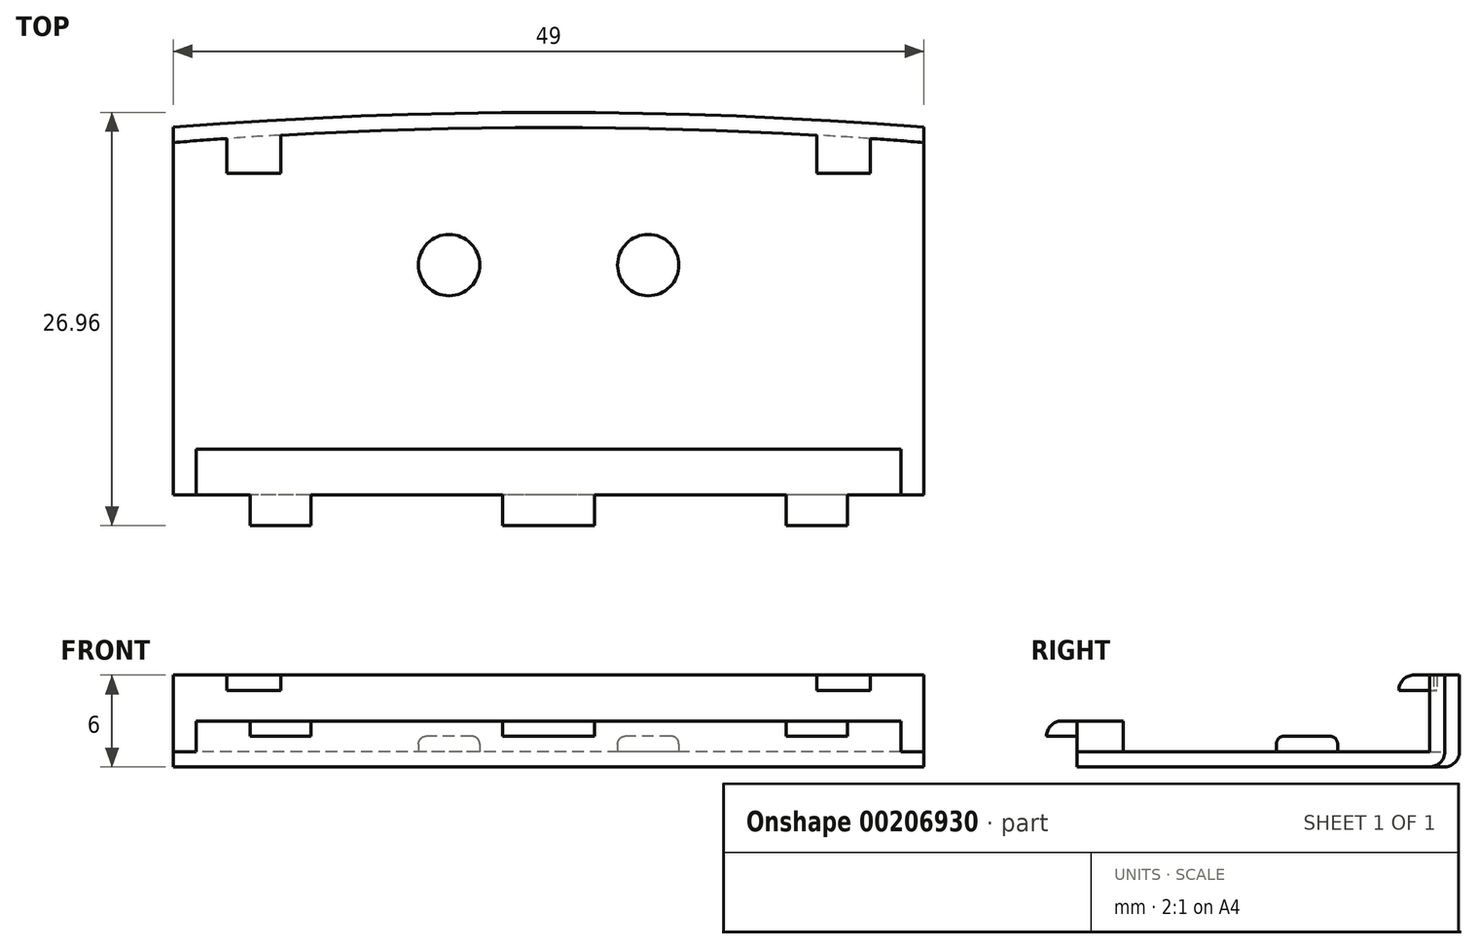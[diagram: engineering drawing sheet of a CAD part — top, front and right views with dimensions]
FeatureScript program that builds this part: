
annotation { "Feature Type Name" : "Feature", "Feature Type Description" : "" }
export const myFeature = defineFeature(function(context is Context, id is Id, definition is map)
    precondition{}
    {
        {
            var Q0;
            Q0=qCreatedBy(makeId("Top.planeOp"),FACE);
            var sketch = newSketch(context, id + "F0", { "sketchPlane" : qUnion([Q0])});
            skLineSegment(sketch, "E0.bottom", {"start": v(24.5, -12) * mm, "end": v(-24.5, -12) * mm});
            skLineSegment(sketch, "E0.left", {"start": v(24.5, -12) * mm, "end": v(24.5, 12) * mm});
            skLineSegment(sketch, "E0.right", {"start": v(-24.5, -12) * mm, "end": v(-24.5, 12) * mm});
            skPoint(sketch, "E0.middle", {"position": v(0, 0) * mm});
            skArc(sketch, "E1", {"start": v(24.5, 12) * mm, "mid": v(0, 12.96) * mm, "end": v(-24.5, 12) * mm});
            skArc(sketch, "E2", {"start": v(24.5, 11) * mm, "mid": v(0, 11.97) * mm, "end": v(-24.5, 11) * mm});
            skLineSegment(sketch, "E3.bottom", {"start": v(23, -9) * mm, "end": v(-23, -9) * mm});
            skLineSegment(sketch, "E3.left", {"start": v(23, -9) * mm, "end": v(23, -15) * mm});
            skLineSegment(sketch, "E3.right", {"start": v(-23, -9) * mm, "end": v(-23, -15) * mm});
            skPoint(sketch, "E3.middle", {"position": v(0, -12) * mm});
            skLineSegment(sketch, "E4.bottom", {"start": v(-16, -14) * mm, "end": v(-19.5, -14) * mm});
            skLineSegment(sketch, "E4.top", {"start": v(-16, -10) * mm, "end": v(-19.5, -10) * mm});
            skLineSegment(sketch, "E4.left", {"start": v(-16, -14) * mm, "end": v(-16, -10) * mm});
            skLineSegment(sketch, "E4.right", {"start": v(-19.5, -14) * mm, "end": v(-19.5, -10) * mm});
            skPoint(sketch, "E4.middle", {"position": v(-17.75, -12) * mm});
            skLineSegment(sketch, "E5.bottom", {"start": v(3, -14) * mm, "end": v(-3, -14) * mm});
            skLineSegment(sketch, "E5.top", {"start": v(3, -10) * mm, "end": v(-3, -10) * mm});
            skLineSegment(sketch, "E5.left", {"start": v(3, -14) * mm, "end": v(3, -10) * mm});
            skLineSegment(sketch, "E5.right", {"start": v(-3, -14) * mm, "end": v(-3, -10) * mm});
            skLineSegment(sketch, "E6.bottom", {"start": v(19.5, -14) * mm, "end": v(16, -14) * mm});
            skLineSegment(sketch, "E6.top", {"start": v(19.5, -10) * mm, "end": v(16, -10) * mm});
            skLineSegment(sketch, "E6.left", {"start": v(19.5, -14) * mm, "end": v(19.5, -10) * mm});
            skLineSegment(sketch, "E6.right", {"start": v(16, -14) * mm, "end": v(16, -10) * mm});
            skPoint(sketch, "E6.middle", {"position": v(17.75, -12) * mm});
            skCircle(sketch, "E7", {"center": v(-6.5, 3) * mm, "radius": 2 * mm});
            skCircle(sketch, "E8", {"center": v(6.5, 3) * mm, "radius": 2 * mm});
            skSolve(sketch);
        }
        {
            var Q0;
            {var subQ0=sQuery(id+"F0.wireOp",EDGE,"E1");Q0=makeQuery(id+"F0.imprint","IMPRINT",FACE,{"disambiguationData":[TD([[makeQuery(id+"F0.imprint","IMPRINT",EDGE,{"derivedFrom":subQ0}),1.0]])]});}
            var Q1;
            {var subQ3=sQuery(id+"F0.wireOp",EDGE,"E2");Q1=makeQuery(id+"F0.imprint","IMPRINT",FACE,{"disambiguationData":[TD([[makeQuery(id+"F0.imprint","IMPRINT",EDGE,{"derivedFrom":subQ3}),1.0]])]});}
            var Q2;
            {var subQ10=sQuery(id+"F0.wireOp",EDGE,"E3.bottom");Q2=makeQuery(id+"F0.imprint","IMPRINT",FACE,{"disambiguationData":[TD([[makeQuery(id+"F0.imprint","IMPRINT",EDGE,{"derivedFrom":subQ10}),1.0]])]});}
            var Q3;
            {var subQ5=sQuery(id+"F0.wireOp",EDGE,"E4.top");Q3=makeQuery(id+"F0.imprint","IMPRINT",FACE,{"disambiguationData":[TD([[makeQuery(id+"F0.imprint","IMPRINT",EDGE,{"derivedFrom":subQ5}),1.0]])]});}
            var Q4;
            {var subQ5=sQuery(id+"F0.wireOp",EDGE,"E5.top");Q4=makeQuery(id+"F0.imprint","IMPRINT",FACE,{"disambiguationData":[TD([[makeQuery(id+"F0.imprint","IMPRINT",EDGE,{"derivedFrom":subQ5}),1.0]])]});}
            var Q5;
            {var subQ5=sQuery(id+"F0.wireOp",EDGE,"E6.top");Q5=makeQuery(id+"F0.imprint","IMPRINT",FACE,{"disambiguationData":[TD([[makeQuery(id+"F0.imprint","IMPRINT",EDGE,{"derivedFrom":subQ5}),1.0]])]});}
            var Q6;
            Q6=makeQuery(id+"F0.imprint","IMPRINT",FACE,{"disambiguationData":[TD([[makeQuery(id+"F0.imprint","IMPRINT",EDGE,{"derivedFrom":sQuery(id+"F0.wireOp",EDGE,"E7")}),1.0]])]});
            var Q7;
            Q7=makeQuery(id+"F0.imprint","IMPRINT",FACE,{"disambiguationData":[TD([[makeQuery(id+"F0.imprint","IMPRINT",EDGE,{"derivedFrom":sQuery(id+"F0.wireOp",EDGE,"E8")}),1.0]])]});
            extrude(context, id + "F1", {"entities" : qUnion([Q0, Q1, Q2, Q3, Q4, Q5, Q6, Q7]), "oppositeDirection" : true, "depth" : 1 * mm});
        }
        {
            var Q0;
            {var subQ10=sQuery(id+"F0.wireOp",EDGE,"E3.bottom");Q0=makeQuery(id+"F0.imprint","IMPRINT",FACE,{"disambiguationData":[TD([[makeQuery(id+"F0.imprint","IMPRINT",EDGE,{"derivedFrom":subQ10}),1.0]])]});}
            var Q1;
            {var subQ5=sQuery(id+"F0.wireOp",EDGE,"E4.top");Q1=makeQuery(id+"F0.imprint","IMPRINT",FACE,{"disambiguationData":[TD([[makeQuery(id+"F0.imprint","IMPRINT",EDGE,{"derivedFrom":subQ5}),1.0]])]});}
            var Q2;
            {var subQ5=sQuery(id+"F0.wireOp",EDGE,"E5.top");Q2=makeQuery(id+"F0.imprint","IMPRINT",FACE,{"disambiguationData":[TD([[makeQuery(id+"F0.imprint","IMPRINT",EDGE,{"derivedFrom":subQ5}),1.0]])]});}
            var Q3;
            {var subQ5=sQuery(id+"F0.wireOp",EDGE,"E6.top");Q3=makeQuery(id+"F0.imprint","IMPRINT",FACE,{"disambiguationData":[TD([[makeQuery(id+"F0.imprint","IMPRINT",EDGE,{"derivedFrom":subQ5}),1.0]])]});}
            extrude(context, id + "F2", {"entities" : qUnion([Q0, Q1, Q2, Q3]), "operationType" : NewBodyOperationType.ADD, "depth" : 2 * mm});
        }
        {
            var Q0;
            {var subQ0=sQuery(id+"F0.wireOp",EDGE,"E0.bottom");Q0=makeQuery(id+"F2.boolean.opBoolean","MERGE",FACE,{"derivedFrom":[makeQuery(id+"F1.opExtrude","SWEPT_FACE",FACE,{"disambiguationData":[OSD([subQ0])]}),makeQuery(id+"F2.opExtrude","SWEPT_FACE",FACE,{"disambiguationData":[OSD([subQ0])]})]});}
            var sketch = newSketch(context, id + "F3", { "sketchPlane" : qUnion([Q0])});
            skLineSegment(sketch, "E9.bottom", {"start": v(-15.5, 1) * mm, "end": v(-19.5, 1) * mm});
            skLineSegment(sketch, "E9.top", {"start": v(-15.5, 3) * mm, "end": v(-19.5, 3) * mm});
            skLineSegment(sketch, "E9.left", {"start": v(-15.5, 1) * mm, "end": v(-15.5, 3) * mm});
            skLineSegment(sketch, "E9.right", {"start": v(-19.5, 1) * mm, "end": v(-19.5, 3) * mm});
            skPoint(sketch, "E9.middle", {"position": v(-17.5, 2) * mm});
            skLineSegment(sketch, "E10.bottom", {"start": v(3, 1) * mm, "end": v(-3, 1) * mm});
            skLineSegment(sketch, "E10.top", {"start": v(3, 3) * mm, "end": v(-3, 3) * mm});
            skLineSegment(sketch, "E10.left", {"start": v(3, 1) * mm, "end": v(3, 3) * mm});
            skLineSegment(sketch, "E10.right", {"start": v(-3, 1) * mm, "end": v(-3, 3) * mm});
            skPoint(sketch, "E10.middle", {"position": v(0, 2) * mm});
            skLineSegment(sketch, "E11.bottom", {"start": v(19.5, 3) * mm, "end": v(15.5, 3) * mm});
            skLineSegment(sketch, "E11.top", {"start": v(19.5, 1) * mm, "end": v(15.5, 1) * mm});
            skLineSegment(sketch, "E11.left", {"start": v(19.5, 3) * mm, "end": v(19.5, 1) * mm});
            skLineSegment(sketch, "E11.right", {"start": v(15.5, 3) * mm, "end": v(15.5, 1) * mm});
            skPoint(sketch, "E11.middle", {"position": v(17.5, 2) * mm});
            skSolve(sketch);
        }
        {
            var Q0;
            {var subQ0=sQuery(id+"F3.wireOp",EDGE,"E9.bottom");Q0=makeQuery(id+"F3.imprint","IMPRINT",FACE,{"disambiguationData":[TD([[makeQuery(id+"F3.imprint","IMPRINT",EDGE,{"derivedFrom":subQ0}),-1.0]])]});}
            var Q1;
            {var subQ0=sQuery(id+"F3.wireOp",EDGE,"E10.bottom");Q1=makeQuery(id+"F3.imprint","IMPRINT",FACE,{"disambiguationData":[TD([[makeQuery(id+"F3.imprint","IMPRINT",EDGE,{"derivedFrom":subQ0}),-1.0]])]});}
            var Q2;
            {var subQ0=sQuery(id+"F3.wireOp",EDGE,"E11.top");Q2=makeQuery(id+"F3.imprint","IMPRINT",FACE,{"disambiguationData":[TD([[makeQuery(id+"F3.imprint","IMPRINT",EDGE,{"derivedFrom":subQ0}),-1.0]])]});}
            extrude(context, id + "F4", {"entities" : qUnion([Q0, Q1, Q2]), "operationType" : NewBodyOperationType.ADD, "depth" : 2 * mm});
        }
        {
            var Q0;
            {var subQ0=sQuery(id+"F0.wireOp",EDGE,"E1");Q0=makeQuery(id+"F0.imprint","IMPRINT",FACE,{"disambiguationData":[TD([[makeQuery(id+"F0.imprint","IMPRINT",EDGE,{"derivedFrom":subQ0}),1.0]])]});}
            extrude(context, id + "F5", {"entities" : qUnion([Q0]), "operationType" : NewBodyOperationType.ADD, "depth" : 5 * mm});
        }
        {
            var Q0;
            Q0=makeQuery(id+"F1.opExtrude","CAP_EDGE",EDGE,{"disambiguationData":[OSD([sQuery(id+"F0.wireOp",EDGE,"E1")])],"isStart":false});
            fillet(context, id + "F6", {"entities" : qUnion([Q0]), "radius" : 1 * mm, "tangentPropagation" : true, "allowEdgeOverflow" : false});
        }
        {
            var Q0;
            Q0=makeQuery(id+"F5.opExtrude","CAP_FACE",FACE,{"disambiguationData":[OSD([sQuery(id+"F0.wireOp",EDGE,"E0.left"),sQuery(id+"F0.wireOp",EDGE,"E0.right"),sQuery(id+"F0.wireOp",EDGE,"E1"),sQuery(id+"F0.wireOp",EDGE,"E2")])],"isStart":false});
            var sketch = newSketch(context, id + "F7", { "sketchPlane" : qUnion([Q0])});
            skLineSegment(sketch, "E12", {"start": v(-24.5, 11) * mm, "end": v(24.5, 11) * mm, "construction": true});
            skLineSegment(sketch, "E13.bottom", {"start": v(-17.5, 9) * mm, "end": v(-21, 9) * mm});
            skLineSegment(sketch, "E13.top", {"start": v(-17.5, 13) * mm, "end": v(-21, 13) * mm});
            skLineSegment(sketch, "E13.left", {"start": v(-17.5, 9) * mm, "end": v(-17.5, 13) * mm});
            skLineSegment(sketch, "E13.right", {"start": v(-21, 9) * mm, "end": v(-21, 13) * mm});
            skPoint(sketch, "E13.middle", {"position": v(-19.25, 11) * mm});
            skLineSegment(sketch, "E14.bottom", {"start": v(17.5, 9) * mm, "end": v(21, 9) * mm});
            skLineSegment(sketch, "E14.top", {"start": v(17.5, 13) * mm, "end": v(21, 13) * mm});
            skLineSegment(sketch, "E14.left", {"start": v(17.5, 9) * mm, "end": v(17.5, 13) * mm});
            skLineSegment(sketch, "E14.right", {"start": v(21, 9) * mm, "end": v(21, 13) * mm});
            skPoint(sketch, "E14.middle", {"position": v(19.25, 11) * mm});
            skSolve(sketch);
        }
        {
            var Q0;
            {var subQ0=sQuery(id+"F7.wireOp",EDGE,"E13.bottom");Q0=makeQuery(id+"F7.imprint","IMPRINT",FACE,{"disambiguationData":[TD([[makeQuery(id+"F7.imprint","IMPRINT",EDGE,{"derivedFrom":subQ0}),-1.0]])]});}
            var Q1;
            {var subQ0=sQuery(id+"F7.wireOp",EDGE,"E13.left");var subQ1=makeQuery(id+"F5.opExtrude","CAP_EDGE",EDGE,{"disambiguationData":[OSD([sQuery(id+"F0.wireOp",EDGE,"E2")])],"isStart":false});var subQ2=makeQuery(id+"F7.imprint","INTERSECT",VERTEX,{"derivedFrom":[subQ1,subQ0]});Q1=makeQuery(id+"F7.imprint","IMPRINT",FACE,{"disambiguationData":[TD([[makeQuery(id+"F7.imprint","IMPRINT",EDGE,{"disambiguationData":[TD([[subQ2,-1.0]])],"derivedFrom":subQ0}),1.0]])]});}
            var Q2;
            {var subQ0=sQuery(id+"F7.wireOp",EDGE,"E14.left");var subQ1=makeQuery(id+"F5.opExtrude","CAP_EDGE",EDGE,{"disambiguationData":[OSD([sQuery(id+"F0.wireOp",EDGE,"E2")])],"isStart":false});var subQ2=makeQuery(id+"F7.imprint","INTERSECT",VERTEX,{"derivedFrom":[subQ1,subQ0]});Q2=makeQuery(id+"F7.imprint","IMPRINT",FACE,{"disambiguationData":[TD([[makeQuery(id+"F7.imprint","IMPRINT",EDGE,{"disambiguationData":[TD([[subQ2,-1.0]])],"derivedFrom":subQ0}),-1.0]])]});}
            var Q3;
            {var subQ0=sQuery(id+"F7.wireOp",EDGE,"E14.bottom");Q3=makeQuery(id+"F7.imprint","IMPRINT",FACE,{"disambiguationData":[TD([[makeQuery(id+"F7.imprint","IMPRINT",EDGE,{"derivedFrom":subQ0}),1.0]])]});}
            extrude(context, id + "F8", {"entities" : qUnion([Q0, Q1, Q2, Q3]), "operationType" : NewBodyOperationType.ADD, "oppositeDirection" : true, "depth" : 1 * mm});
        }
        {
            var Q0;
            Q0=makeQuery(id+"F0.imprint","IMPRINT",FACE,{"disambiguationData":[TD([[makeQuery(id+"F0.imprint","IMPRINT",EDGE,{"derivedFrom":sQuery(id+"F0.wireOp",EDGE,"E7")}),1.0]])]});
            var Q1;
            Q1=makeQuery(id+"F0.imprint","IMPRINT",FACE,{"disambiguationData":[TD([[makeQuery(id+"F0.imprint","IMPRINT",EDGE,{"derivedFrom":sQuery(id+"F0.wireOp",EDGE,"E8")}),1.0]])]});
            extrude(context, id + "F9", {"entities" : qUnion([Q0, Q1]), "depth" : 1 * mm});
        }
        {
            var Q0;
            Q0=makeQuery(id+"F9.opExtrude","CAP_EDGE",EDGE,{"disambiguationData":[OSD([sQuery(id+"F0.wireOp",EDGE,"E7")])],"isStart":false});
            var Q1;
            Q1=makeQuery(id+"F9.opExtrude","CAP_EDGE",EDGE,{"disambiguationData":[OSD([sQuery(id+"F0.wireOp",EDGE,"E8")])],"isStart":false});
            fillet(context, id + "F10", {"entities" : qUnion([Q0, Q1]), "radius" : 0.5 * mm, "tangentPropagation" : true, "allowEdgeOverflow" : false});
        }
        {
            var Q0;
            {var subQ0=sQuery(id+"F0.wireOp",EDGE,"E0.bottom");var subQ1=makeQuery(id+"F2.opExtrude","CAP_EDGE",EDGE,{"disambiguationData":[OSD([subQ0])],"isStart":false});Q0=makeQuery(id+"F4.opExtrude","CAP_EDGE",EDGE,{"disambiguationData":[OSD([subQ0]),TDD([makeQuery(id+"F3.imprint","IMPRINT",EDGE,{"disambiguationData":[TD([[makeQuery(id+"F3.imprint","INTERSECT",VERTEX,{"derivedFrom":[subQ1,sQuery(id+"F3.wireOp",EDGE,"E9.left")]}),-1.0]])],"derivedFrom":subQ1})])],"isStart":false});}
            var Q1;
            {var subQ0=sQuery(id+"F0.wireOp",EDGE,"E0.bottom");var subQ1=makeQuery(id+"F2.opExtrude","CAP_EDGE",EDGE,{"disambiguationData":[OSD([subQ0])],"isStart":false});Q1=makeQuery(id+"F4.opExtrude","CAP_EDGE",EDGE,{"disambiguationData":[OSD([subQ0]),TDD([makeQuery(id+"F3.imprint","IMPRINT",EDGE,{"disambiguationData":[TD([[makeQuery(id+"F3.imprint","INTERSECT",VERTEX,{"derivedFrom":[subQ1,sQuery(id+"F3.wireOp",EDGE,"E10.left")]}),-1.0]])],"derivedFrom":subQ1})])],"isStart":false});}
            var Q2;
            {var subQ0=sQuery(id+"F0.wireOp",EDGE,"E0.bottom");var subQ1=makeQuery(id+"F2.opExtrude","CAP_EDGE",EDGE,{"disambiguationData":[OSD([subQ0])],"isStart":false});Q2=makeQuery(id+"F4.opExtrude","CAP_EDGE",EDGE,{"disambiguationData":[OSD([subQ0]),TDD([makeQuery(id+"F3.imprint","IMPRINT",EDGE,{"disambiguationData":[TD([[makeQuery(id+"F3.imprint","INTERSECT",VERTEX,{"derivedFrom":[subQ1,sQuery(id+"F3.wireOp",EDGE,"E11.left")]}),-1.0]])],"derivedFrom":subQ1})])],"isStart":false});}
            var Q3;
            Q3=makeQuery(id+"F8.opExtrude","CAP_EDGE",EDGE,{"disambiguationData":[OSD([sQuery(id+"F7.wireOp",EDGE,"E13.bottom")])],"isStart":true});
            var Q4;
            Q4=makeQuery(id+"F8.opExtrude","CAP_EDGE",EDGE,{"disambiguationData":[OSD([sQuery(id+"F7.wireOp",EDGE,"E14.bottom")])],"isStart":true});
            fillet(context, id + "F11", {"entities" : qUnion([Q0, Q1, Q2, Q3, Q4]), "radius" : 1 * mm, "tangentPropagation" : true, "allowEdgeOverflow" : false});
        }
    });
